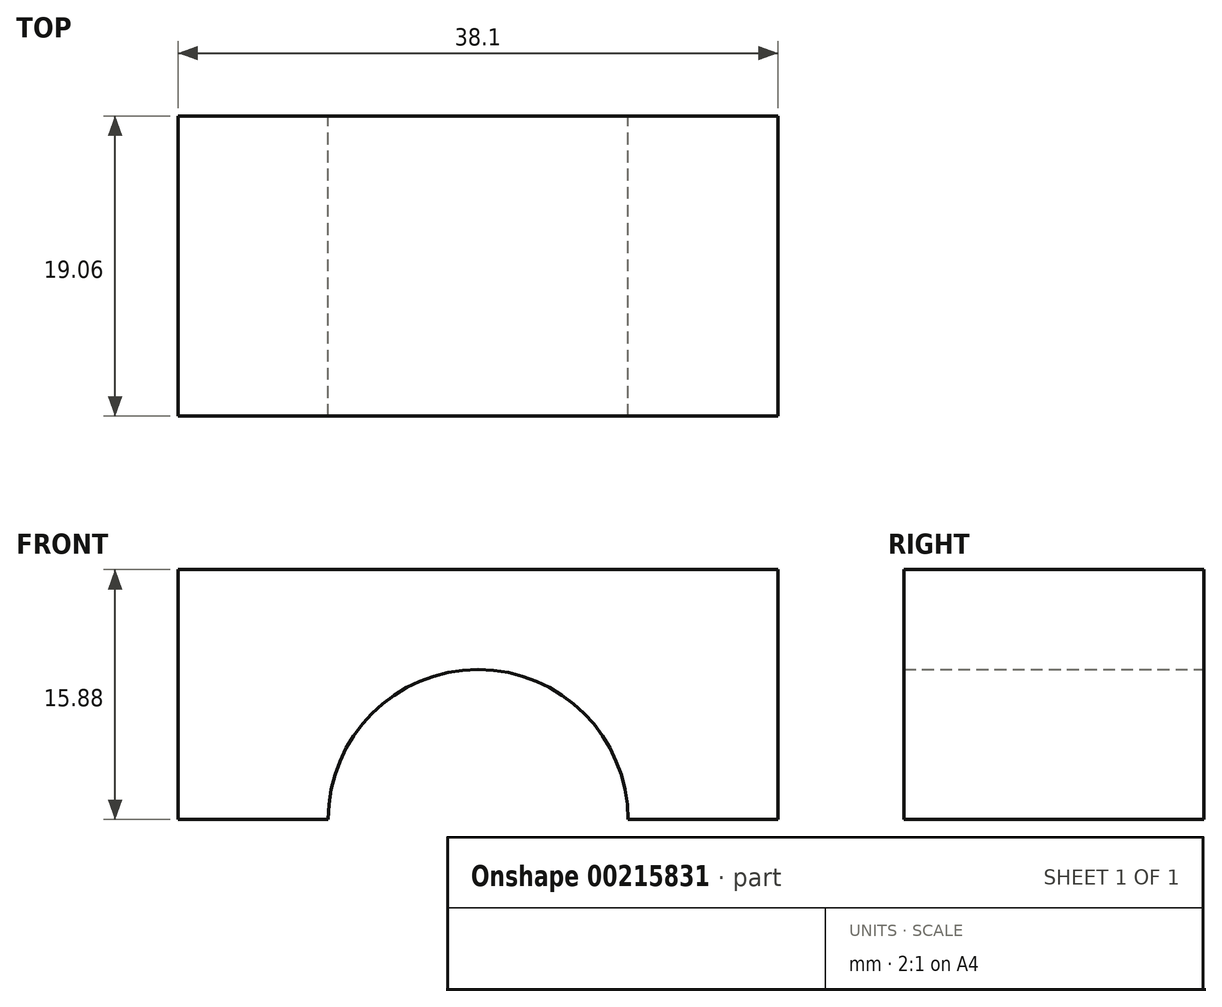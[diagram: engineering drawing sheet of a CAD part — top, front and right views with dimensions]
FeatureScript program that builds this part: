
annotation { "Feature Type Name" : "Feature", "Feature Type Description" : "" }
export const myFeature = defineFeature(function(context is Context, id is Id, definition is map)
    precondition{}
    {
        {
            var Q0;
            Q0=qCreatedBy(makeId("Front.planeOp"),FACE);
            var sketch = newSketch(context, id + "F0", { "sketchPlane" : qUnion([Q0])});
            skLineSegment(sketch, "E0", {"start": v(-19.05, 0) * mm, "end": v(-9.53, 0) * mm});
            skLineSegment(sketch, "E1", {"start": v(-19.05, 0) * mm, "end": v(-19.05, 15.87) * mm});
            skLineSegment(sketch, "E2", {"start": v(-19.05, 15.87) * mm, "end": v(0, 15.87) * mm});
            skArc(sketch, "E3", {"start": v(-9.53, 0) * mm, "mid": v(-6.74, 6.74) * mm, "end": v(0, 9.53) * mm});
            skArc(sketch, "E4.MirrorCS", {"start": v(9.53, 0) * mm, "mid": v(6.74, 6.74) * mm, "end": v(0, 9.53) * mm});
            skLineSegment(sketch, "E5.MirrorCS", {"start": v(19.05, 0) * mm, "end": v(9.53, 0) * mm});
            skLineSegment(sketch, "E6.MirrorCS", {"start": v(19.05, 0) * mm, "end": v(19.05, 15.87) * mm});
            skLineSegment(sketch, "E7.MirrorCS", {"start": v(19.05, 15.87) * mm, "end": v(0, 15.87) * mm});
            skSolve(sketch);
        }
        {
            var Q0;
            Q0=qSketchRegion(id+"F0",true);
            extrude(context, id + "F1", {"entities" : qUnion([Q0]), "endBound" : BoundingType.SYMMETRIC, "depth" : 19.05 * mm});
        }
    });
